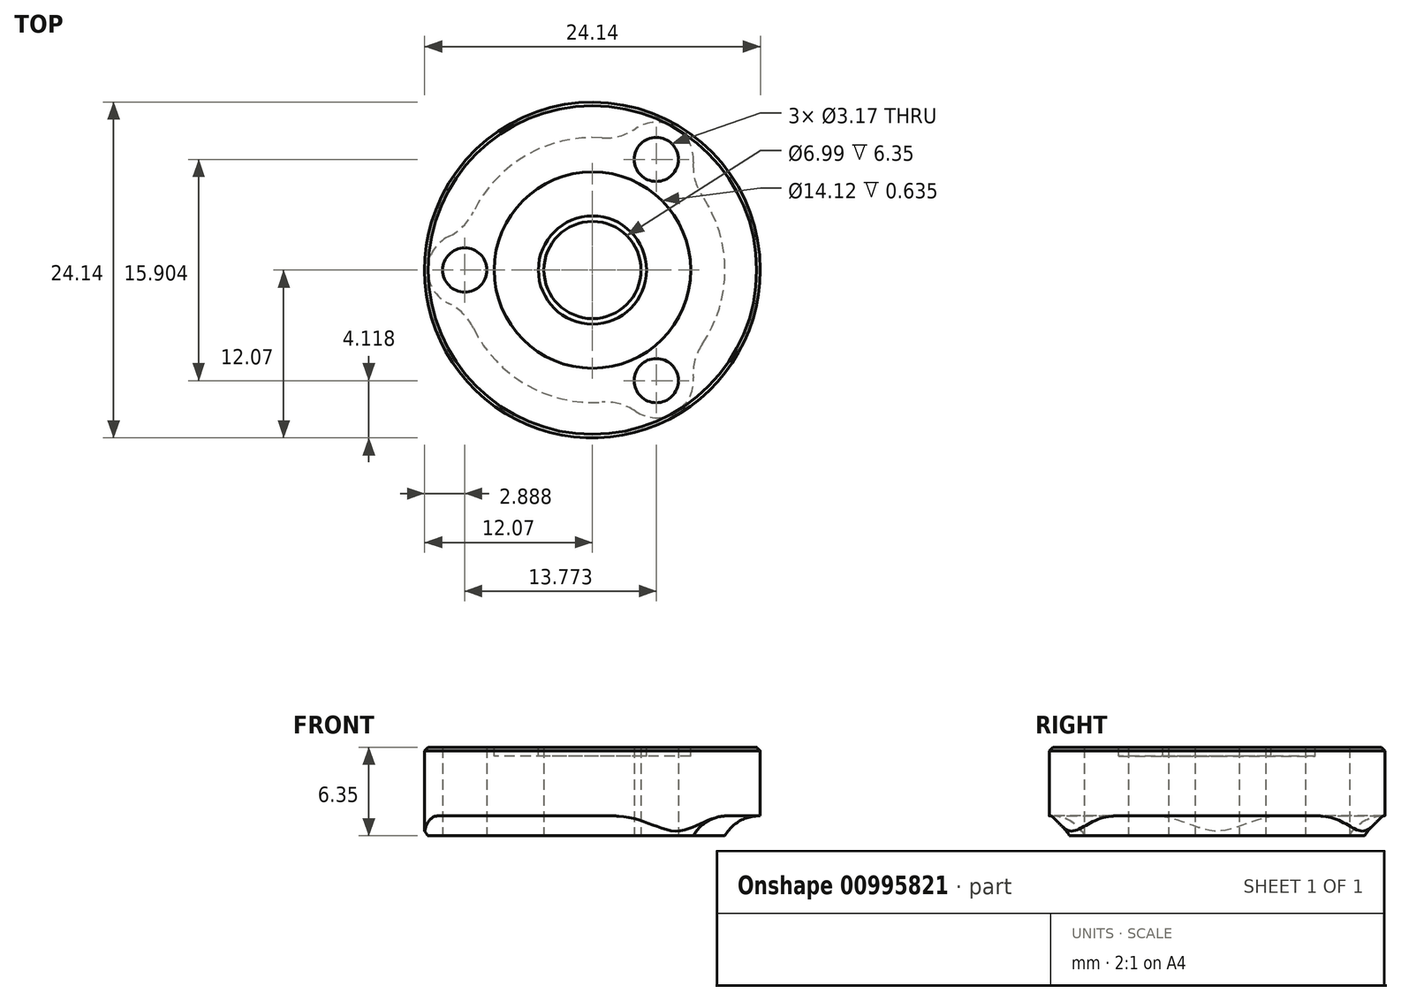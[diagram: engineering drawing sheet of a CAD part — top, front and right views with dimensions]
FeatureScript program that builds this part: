
annotation { "Feature Type Name" : "Feature", "Feature Type Description" : "" }
export const myFeature = defineFeature(function(context is Context, id is Id, definition is map)
    precondition{}
    {
        {
            var Q0;
            Q0=qCreatedBy(makeId("Top.planeOp"),FACE);
            var sketch = newSketch(context, id + "F0", { "sketchPlane" : qUnion([Q0])});
            skCircle(sketch, "E0", {"center": v(0, 0) * mm, "radius": 3.5 * mm});
            skCircle(sketch, "E1", {"center": v(0, 0) * mm, "radius": 3.89 * mm});
            skCircle(sketch, "E2", {"center": v(0, 0) * mm, "radius": 9.18 * mm, "construction": true});
            skLineSegment(sketch, "E3", {"start": v(0, 0) * mm, "end": v(-23, 0) * mm, "construction": true});
            skCircle(sketch, "E4", {"center": v(-9.18, 0) * mm, "radius": 1.59 * mm});
            skCircle(sketch, "E5.1.0", {"center": v(4.6, 7.95) * mm, "radius": 1.59 * mm});
            skCircle(sketch, "E5.2.0", {"center": v(4.6, -7.95) * mm, "radius": 1.59 * mm});
            skLineSegment(sketch, "E5.anchor1", {"start": v(0, 0) * mm, "end": v(-9.18, 0) * mm, "construction": true});
            skLineSegment(sketch, "E5.anchor2", {"start": v(0, 0) * mm, "end": v(4.6, -7.95) * mm, "construction": true});
            skCircle(sketch, "E6", {"center": v(0, 0) * mm, "radius": 12.07 * mm});
            skSolve(sketch);
        }
        {
            var Q0;
            Q0=makeQuery(id+"F0.imprint","IMPRINT",FACE,{"disambiguationData":[TD([[makeQuery(id+"F0.imprint","IMPRINT",EDGE,{"derivedFrom":sQuery(id+"F0.wireOp",EDGE,"E1")}),1.0]])]});
            var Q1;
            Q1=makeQuery(id+"F0.imprint","IMPRINT",FACE,{"disambiguationData":[TD([[makeQuery(id+"F0.imprint","IMPRINT",EDGE,{"derivedFrom":sQuery(id+"F0.wireOp",EDGE,"E1")}),-1.0]])]});
            extrude(context, id + "F1", {"entities" : qUnion([Q0, Q1]), "depth" : 6.35 * mm, "offsetDistance" : 25.4 * mm});
        }
        {
            var Q0;
            Q0=makeQuery(id+"F1.opExtrude","CAP_FACE",FACE,{"disambiguationData":[OSD([sQuery(id+"F0.wireOp",EDGE,"E4"),sQuery(id+"F0.wireOp",EDGE,"E5.1.0"),sQuery(id+"F0.wireOp",EDGE,"E5.2.0"),sQuery(id+"F0.wireOp",EDGE,"E0"),sQuery(id+"F0.wireOp",EDGE,"E6")])],"isStart":false});
            var sketch = newSketch(context, id + "F2", { "sketchPlane" : qUnion([Q0])});
            skCircle(sketch, "E7", {"center": v(0, 0) * mm, "radius": 3.89 * mm});
            skCircle(sketch, "E8", {"center": v(0, 0) * mm, "radius": 7.06 * mm});
            skSolve(sketch);
        }
        {
            var Q0;
            Q0=makeQuery(id+"F2.imprint","IMPRINT",FACE,{"disambiguationData":[TD([[makeQuery(id+"F2.imprint","IMPRINT",EDGE,{"derivedFrom":sQuery(id+"F2.wireOp",EDGE,"E7")}),-1.0]])]});
            extrude(context, id + "F3", {"entities" : qUnion([Q0]), "operationType" : NewBodyOperationType.REMOVE, "oppositeDirection" : true, "depth" : 0.64 * mm, "offsetDistance" : 25.4 * mm});
        }
        {
            var Q0;
            Q0=makeQuery(id+"F3.boolean.opBoolean","COPY",EDGE,{"derivedFrom":makeQuery(id+"F3.opExtrude","CAP_EDGE",EDGE,{"disambiguationData":[OSD([sQuery(id+"F2.wireOp",EDGE,"E8")])],"isStart":true})});
            var Q1;
            Q1=makeQuery(id+"F1.opExtrude","CAP_EDGE",EDGE,{"disambiguationData":[OSD([sQuery(id+"F0.wireOp",EDGE,"E6")])],"isStart":false});
            chamfer(context, id + "F4", {"entities" : qUnion([Q0, Q1]), "width" : 0.25 * mm, "tangentPropagation" : true});
        }
        {
            var Q0;
            Q0=makeQuery(id+"F1.opExtrude","CAP_FACE",FACE,{"disambiguationData":[OSD([sQuery(id+"F0.wireOp",EDGE,"E4"),sQuery(id+"F0.wireOp",EDGE,"E5.1.0"),sQuery(id+"F0.wireOp",EDGE,"E5.2.0"),sQuery(id+"F0.wireOp",EDGE,"E0"),sQuery(id+"F0.wireOp",EDGE,"E6")])],"isStart":true});
            var sketch = newSketch(context, id + "F5", { "sketchPlane" : qUnion([Q0])});
            skArc(sketch, "E9", {"start": v(-8.56, -4.17) * mm, "mid": v(-4.76, -8.25) * mm, "end": v(0.67, -9.5) * mm});
            skArc(sketch, "E10", {"start": v(-10.34, 2.4) * mm, "mid": v(-11.85, 0) * mm, "end": v(-10.34, -2.4) * mm});
            skArc(sketch, "E11.1.0", {"start": v(3.09, -10.15) * mm, "mid": v(5.92, -10.26) * mm, "end": v(7.25, -7.75) * mm});
            skArc(sketch, "E11.2.0", {"start": v(7.25, 7.75) * mm, "mid": v(5.92, 10.26) * mm, "end": v(3.09, 10.15) * mm});
            skArc(sketch, "E11.2.1", {"start": v(0.67, 9.5) * mm, "mid": v(-4.76, 8.25) * mm, "end": v(-8.56, 4.17) * mm});
            skArc(sketch, "E12.trimOffspring", {"start": v(7.9, -5.33) * mm, "mid": v(9.53, 0) * mm, "end": v(7.9, 5.33) * mm});
            skArc(sketch, "E13.trimOffspring", {"start": v(7.9, -5.33) * mm, "mid": v(9.52, 0) * mm, "end": v(7.9, 5.33) * mm});
            skPoint(sketch, "E14.visualSharp", {"position": v(-9.14, 2.67) * mm});
            skArc(sketch, "E14.filletArc", {"start": v(-10.34, 2.4) * mm, "mid": v(-9.3, 3.14) * mm, "end": v(-8.56, 4.17) * mm});
            skPoint(sketch, "E15.visualSharp", {"position": v(-9.14, -2.67) * mm});
            skArc(sketch, "E15.filletArc", {"start": v(-8.56, -4.17) * mm, "mid": v(-9.3, -3.14) * mm, "end": v(-10.34, -2.4) * mm});
            skPoint(sketch, "E16.visualSharp", {"position": v(2.26, -9.25) * mm});
            skArc(sketch, "E16.filletArc", {"start": v(3.09, -10.15) * mm, "mid": v(1.93, -9.62) * mm, "end": v(0.67, -9.5) * mm});
            skPoint(sketch, "E17.visualSharp", {"position": v(6.88, -6.59) * mm});
            skArc(sketch, "E17.filletArc", {"start": v(7.9, -5.33) * mm, "mid": v(7.37, -6.49) * mm, "end": v(7.25, -7.75) * mm});
            skPoint(sketch, "E18.visualSharp", {"position": v(6.88, 6.59) * mm});
            skArc(sketch, "E18.filletArc", {"start": v(7.25, 7.75) * mm, "mid": v(7.37, 6.49) * mm, "end": v(7.9, 5.33) * mm});
            skPoint(sketch, "E19.visualSharp", {"position": v(2.26, 9.25) * mm});
            skArc(sketch, "E19.filletArc", {"start": v(0.67, 9.5) * mm, "mid": v(1.93, 9.62) * mm, "end": v(3.09, 10.15) * mm});
            skSolve(sketch);
        }
        {
            var Q0;
            Q0=makeQuery(id+"F5.imprint","IMPRINT",FACE,{"disambiguationData":[TD([[makeQuery(id+"F5.imprint","IMPRINT",EDGE,{"derivedFrom":sQuery(id+"F5.wireOp",EDGE,"E10")}),-1.0]])]});
            extrude(context, id + "F6", {"entities" : qUnion([Q0]), "operationType" : NewBodyOperationType.REMOVE, "oppositeDirection" : true, "depth" : 1.42 * mm, "offsetDistance" : 25.4 * mm});
        }
        {
            var Q0;
            Q0=makeQuery(id+"F6.boolean.opBoolean","COPY",EDGE,{"derivedFrom":makeQuery(id+"F6.opExtrude","CAP_EDGE",EDGE,{"disambiguationData":[OSD([sQuery(id+"F5.wireOp",EDGE,"E12.trimOffspring")])],"isStart":false})});
            var Q1;
            Q1=makeQuery(id+"F6.boolean.opBoolean","COPY",EDGE,{"derivedFrom":makeQuery(id+"F6.opExtrude","CAP_EDGE",EDGE,{"disambiguationData":[OSD([sQuery(id+"F5.wireOp",EDGE,"E17.filletArc")])],"isStart":false})});
            var Q2;
            Q2=makeQuery(id+"F6.boolean.opBoolean","COPY",EDGE,{"derivedFrom":makeQuery(id+"F6.opExtrude","CAP_EDGE",EDGE,{"disambiguationData":[OSD([sQuery(id+"F5.wireOp",EDGE,"E11.1.0")])],"isStart":false})});
            var Q3;
            Q3=makeQuery(id+"F6.boolean.opBoolean","COPY",EDGE,{"derivedFrom":makeQuery(id+"F6.opExtrude","CAP_EDGE",EDGE,{"disambiguationData":[OSD([sQuery(id+"F5.wireOp",EDGE,"E18.filletArc")])],"isStart":false})});
            var Q4;
            Q4=makeQuery(id+"F6.boolean.opBoolean","COPY",EDGE,{"derivedFrom":makeQuery(id+"F6.opExtrude","CAP_EDGE",EDGE,{"disambiguationData":[OSD([sQuery(id+"F5.wireOp",EDGE,"E11.2.0")])],"isStart":false})});
            var Q5;
            Q5=makeQuery(id+"F6.boolean.opBoolean","COPY",EDGE,{"derivedFrom":makeQuery(id+"F6.opExtrude","CAP_EDGE",EDGE,{"disambiguationData":[OSD([sQuery(id+"F5.wireOp",EDGE,"E9")])],"isStart":false})});
            var Q6;
            Q6=makeQuery(id+"F6.boolean.opBoolean","COPY",EDGE,{"derivedFrom":makeQuery(id+"F6.opExtrude","CAP_EDGE",EDGE,{"disambiguationData":[OSD([sQuery(id+"F5.wireOp",EDGE,"E16.filletArc")])],"isStart":false})});
            var Q7;
            Q7=makeQuery(id+"F6.boolean.opBoolean","COPY",EDGE,{"derivedFrom":makeQuery(id+"F6.opExtrude","CAP_EDGE",EDGE,{"disambiguationData":[OSD([sQuery(id+"F5.wireOp",EDGE,"E19.filletArc")])],"isStart":false})});
            var Q8;
            Q8=makeQuery(id+"F6.boolean.opBoolean","COPY",EDGE,{"derivedFrom":makeQuery(id+"F6.opExtrude","CAP_EDGE",EDGE,{"disambiguationData":[OSD([sQuery(id+"F5.wireOp",EDGE,"E11.2.1")])],"isStart":false})});
            var Q9;
            Q9=makeQuery(id+"F6.boolean.opBoolean","COPY",EDGE,{"derivedFrom":makeQuery(id+"F6.opExtrude","CAP_EDGE",EDGE,{"disambiguationData":[OSD([sQuery(id+"F5.wireOp",EDGE,"E15.filletArc")])],"isStart":false})});
            var Q10;
            Q10=makeQuery(id+"F6.boolean.opBoolean","COPY",EDGE,{"derivedFrom":makeQuery(id+"F6.opExtrude","CAP_EDGE",EDGE,{"disambiguationData":[OSD([sQuery(id+"F5.wireOp",EDGE,"E10")])],"isStart":false})});
            fillet(context, id + "F7", {"entities" : qUnion([Q0, Q1, Q2, Q3, Q4, Q5, Q6, Q7, Q8, Q9, Q10]), "radius" : 2.8 * mm, "tangentPropagation" : true, "allowEdgeOverflow" : false});
        }
    });
